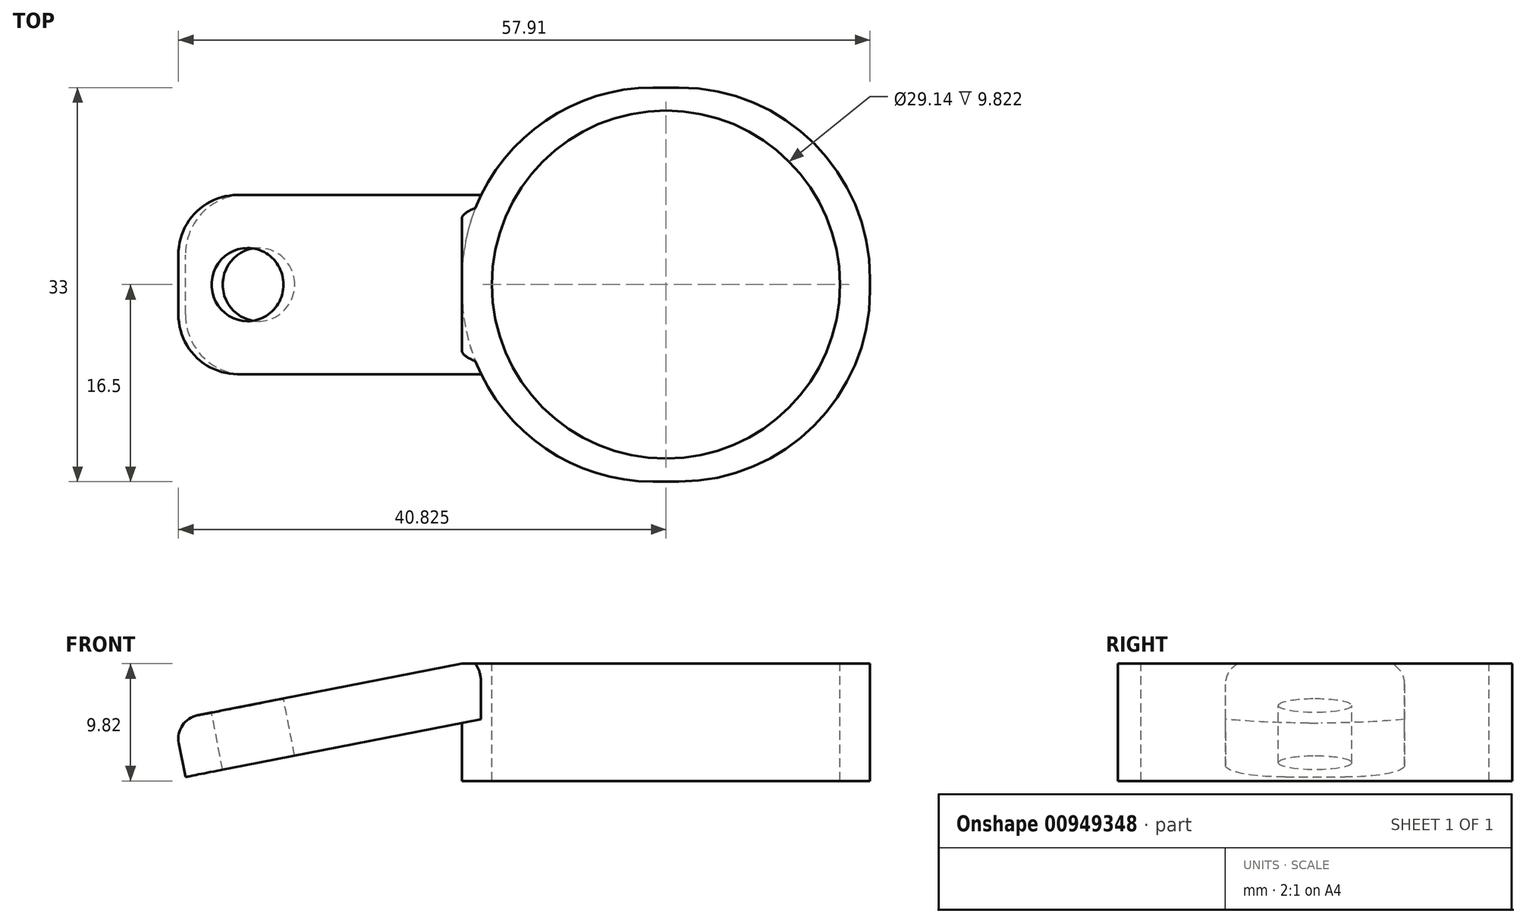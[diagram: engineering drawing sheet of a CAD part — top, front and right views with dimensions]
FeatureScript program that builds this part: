
annotation { "Feature Type Name" : "Feature", "Feature Type Description" : "" }
export const myFeature = defineFeature(function(context is Context, id is Id, definition is map)
    precondition{}
    {
        {
            var Q0;
            Q0=qCreatedBy(makeId("Front.planeOp"),FACE);
            var sketch = newSketch(context, id + "F0", { "sketchPlane" : qUnion([Q0])});
            skLineSegment(sketch, "E0", {"start": v(-73.39, 23.49) * mm, "end": v(-49.3, 28.19) * mm});
            skLineSegment(sketch, "E1", {"start": v(-49.3, 28.19) * mm, "end": v(-15.13, 28.19) * mm});
            skLineSegment(sketch, "E2", {"start": v(-15.13, 28.19) * mm, "end": v(-15.13, 18.37) * mm});
            skLineSegment(sketch, "E3", {"start": v(-15.13, 18.37) * mm, "end": v(-49.3, 18.37) * mm});
            skLineSegment(sketch, "E4", {"start": v(-49.3, 18.37) * mm, "end": v(-49.3, 28.19) * mm});
            skLineSegment(sketch, "E5", {"start": v(-73.39, 23.49) * mm, "end": v(-72.45, 18.7) * mm});
            skLineSegment(sketch, "E6", {"start": v(-72.45, 18.7) * mm, "end": v(-49.3, 23.22) * mm});
            skLineSegment(sketch, "E7", {"start": v(-32.22, 28.19) * mm, "end": v(-32.22, 26.7) * mm});
            skSolve(sketch);
        }
        {
            var Q0;
            {var subQ3=sQuery(id+"F0.wireOp",EDGE,"E1");Q0=makeQuery(id+"F0.imprint","IMPRINT",FACE,{"disambiguationData":[TD([[makeQuery(id+"F0.imprint","IMPRINT",EDGE,{"derivedFrom":subQ3}),-1.0]])]});}
            extrude(context, id + "F1", {"entities" : qUnion([Q0]), "endBound" : BoundingType.SYMMETRIC, "depth" : 33 * mm, "offsetDistance" : 25 * mm});
        }
        {
            var Q0;
            {var subQ0=sQuery(id+"F0.wireOp",EDGE,"E0");Q0=makeQuery(id+"F0.imprint","IMPRINT",FACE,{"disambiguationData":[TD([[makeQuery(id+"F0.imprint","IMPRINT",EDGE,{"derivedFrom":subQ0}),-1.0]])]});}
            extrude(context, id + "F2", {"entities" : qUnion([Q0]), "operationType" : NewBodyOperationType.ADD, "endBound" : BoundingType.SYMMETRIC, "depth" : 15 * mm, "offsetDistance" : 25 * mm});
        }
        {
            var Q0;
            Q0=makeQuery(id+"F1.opExtrude","CAP_EDGE",EDGE,{"disambiguationData":[OSD([sQuery(id+"F0.wireOp",EDGE,"E2")])],"isStart":true});
            var Q1;
            Q1=makeQuery(id+"F1.opExtrude","CAP_EDGE",EDGE,{"disambiguationData":[OSD([sQuery(id+"F0.wireOp",EDGE,"E2")])],"isStart":false});
            var Q2;
            Q2=makeQuery(id+"F1.opExtrude","CAP_EDGE",EDGE,{"disambiguationData":[OSD([sQuery(id+"F0.wireOp",EDGE,"E4")])],"isStart":false});
            var Q3;
            Q3=makeQuery(id+"F1.opExtrude","CAP_EDGE",EDGE,{"disambiguationData":[OSD([sQuery(id+"F0.wireOp",EDGE,"E4")])],"isStart":true});
            fillet(context, id + "F3", {"entities" : qUnion([Q0, Q1, Q2, Q3]), "radius" : 16 * mm, "tangentPropagation" : true, "allowEdgeOverflow" : false});
        }
        {
            var Q0;
            Q0=makeQuery(id+"F1.opExtrude","SWEPT_FACE",FACE,{"disambiguationData":[OSD([sQuery(id+"F0.wireOp",EDGE,"E1")])]});
            var sketch = newSketch(context, id + "F4", { "sketchPlane" : qUnion([Q0])});
            skCircle(sketch, "E8", {"center": v(-32.22, 0) * mm, "radius": 14.57 * mm});
            skPoint(sketch, "E8.centerSnap0", {"position": v(-32.22, 16.5) * mm});
            skSolve(sketch);
        }
        {
            var Q0;
            Q0=makeQuery(id+"F4.imprint","IMPRINT",FACE,{"disambiguationData":[TD([[makeQuery(id+"F4.imprint","IMPRINT",EDGE,{"derivedFrom":sQuery(id+"F4.wireOp",EDGE,"E8")}),1.0]])]});
            extrude(context, id + "F5", {"entities" : qUnion([Q0]), "operationType" : NewBodyOperationType.REMOVE, "oppositeDirection" : true, "depth" : 13 * mm, "offsetDistance" : 25 * mm});
        }
        {
            var Q0;
            Q0=makeQuery(id+"F2.opExtrude","SWEPT_FACE",FACE,{"disambiguationData":[OSD([sQuery(id+"F0.wireOp",EDGE,"E0")])]});
            var sketch = newSketch(context, id + "F6", { "sketchPlane" : qUnion([Q0])});
            skCircle(sketch, "E9", {"center": v(-61.28, 0) * mm, "radius": 3.07 * mm});
            skSolve(sketch);
        }
        {
            var Q0;
            Q0=makeQuery(id+"F6.imprint","IMPRINT",FACE,{"disambiguationData":[TD([[makeQuery(id+"F6.imprint","IMPRINT",EDGE,{"derivedFrom":sQuery(id+"F6.wireOp",EDGE,"E9")}),1.0]])]});
            extrude(context, id + "F7", {"entities" : qUnion([Q0]), "operationType" : NewBodyOperationType.REMOVE, "depth" : -25 * mm, "offsetDistance" : 25 * mm});
        }
        {
            var Q0;
            Q0=makeQuery(id+"F2.opExtrude","CAP_EDGE",EDGE,{"disambiguationData":[OSD([sQuery(id+"F0.wireOp",EDGE,"E0")])],"isStart":false});
            var Q1;
            Q1=makeQuery(id+"F2.opExtrude","SWEPT_EDGE",EDGE,{"disambiguationData":[OSD([sQuery(id+"F0.wireOp",EDGE,"E0"),sQuery(id+"F0.wireOp",EDGE,"E5")])]});
            var Q2;
            Q2=makeQuery(id+"F2.opExtrude","CAP_EDGE",EDGE,{"disambiguationData":[OSD([sQuery(id+"F0.wireOp",EDGE,"E0")])],"isStart":true});
            fillet(context, id + "F8", {"entities" : qUnion([Q0, Q1, Q2]), "radius" : 2 * mm, "tangentPropagation" : true, "allowEdgeOverflow" : false});
        }
        {
            var Q0;
            Q0=makeQuery(id+"F2.opExtrude","CAP_EDGE",EDGE,{"disambiguationData":[OSD([sQuery(id+"F0.wireOp",EDGE,"E5")])],"isStart":true});
            var Q1;
            Q1=makeQuery(id+"F2.opExtrude","CAP_EDGE",EDGE,{"disambiguationData":[OSD([sQuery(id+"F0.wireOp",EDGE,"E5")])],"isStart":false});
            fillet(context, id + "F9", {"entities" : qUnion([Q0, Q1]), "radius" : 5 * mm, "tangentPropagation" : true, "allowEdgeOverflow" : false});
        }
    });
